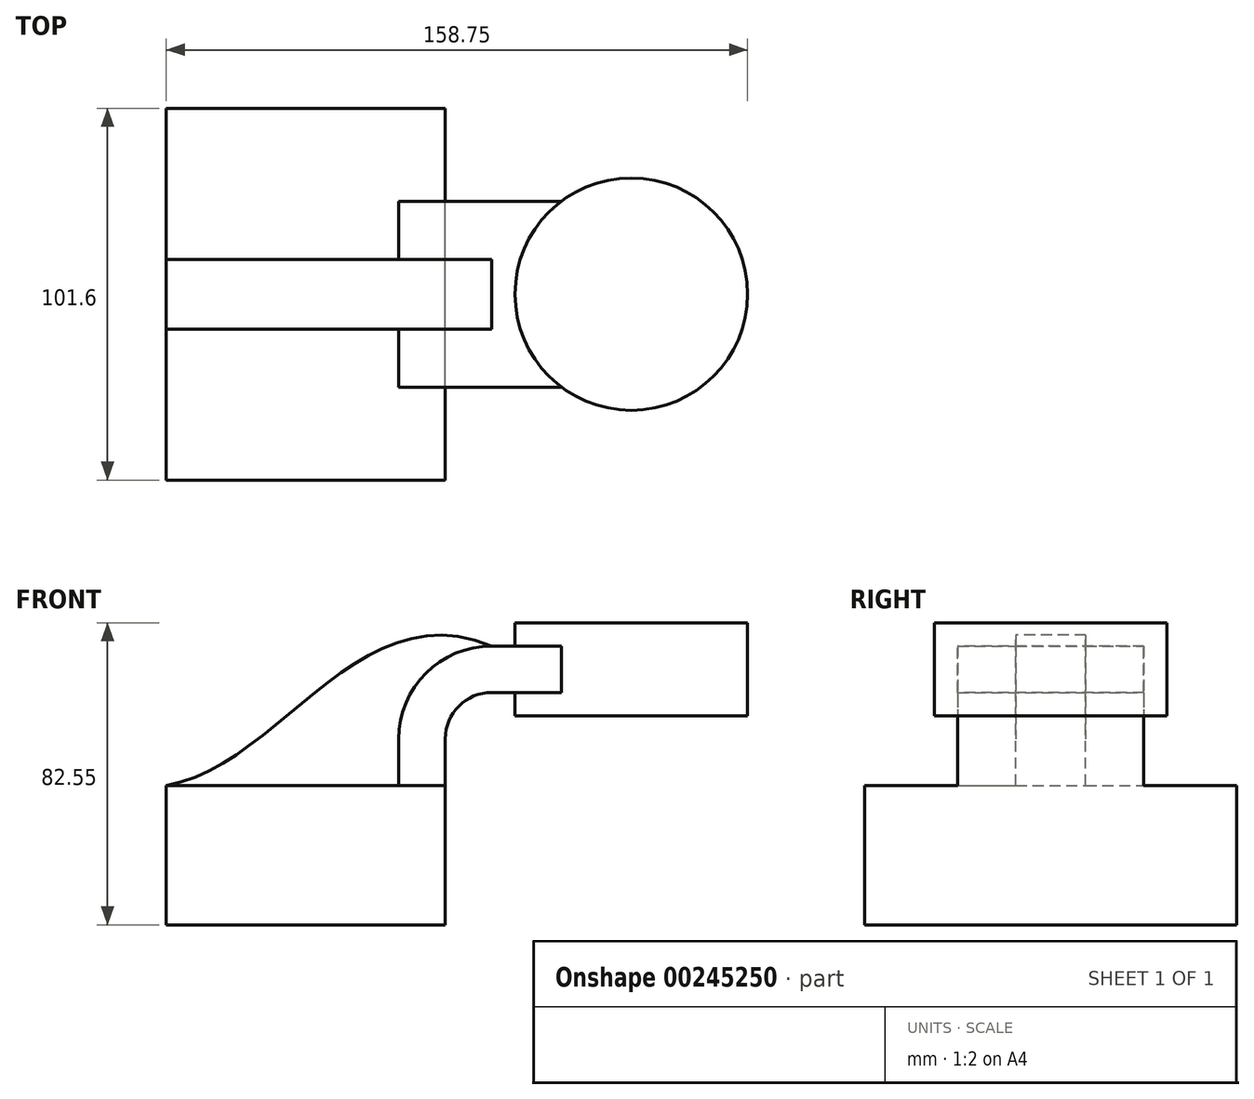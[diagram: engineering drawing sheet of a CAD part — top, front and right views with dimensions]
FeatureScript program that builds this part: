
annotation { "Feature Type Name" : "Feature", "Feature Type Description" : "" }
export const myFeature = defineFeature(function(context is Context, id is Id, definition is map)
    precondition{}
    {
        {
            var Q0;
            Q0=qCreatedBy(makeId("Front.planeOp"),FACE);
            var sketch = newSketch(context, id + "F0", { "sketchPlane" : qUnion([Q0])});
            skLineSegment(sketch, "E0.bottom", {"start": v(38.1, -19.05) * mm, "end": v(-38.1, -19.05) * mm});
            skLineSegment(sketch, "E0.top", {"start": v(38.1, 19.05) * mm, "end": v(-38.1, 19.05) * mm});
            skLineSegment(sketch, "E0.left", {"start": v(38.1, -19.05) * mm, "end": v(38.1, 19.05) * mm});
            skLineSegment(sketch, "E0.right", {"start": v(-38.1, -19.05) * mm, "end": v(-38.1, 19.05) * mm});
            skPoint(sketch, "E0.middle", {"position": v(0, 0) * mm});
            skLineSegment(sketch, "E1.bottom", {"start": v(120.65, 38.1) * mm, "end": v(57.15, 38.1) * mm});
            skLineSegment(sketch, "E1.top", {"start": v(120.65, 63.5) * mm, "end": v(57.15, 63.5) * mm});
            skLineSegment(sketch, "E1.left", {"start": v(120.65, 38.1) * mm, "end": v(120.65, 63.5) * mm});
            skLineSegment(sketch, "E1.right", {"start": v(57.15, 38.1) * mm, "end": v(57.15, 63.5) * mm});
            skPoint(sketch, "E1.middle", {"position": v(88.9, 50.8) * mm});
            skLineSegment(sketch, "E2", {"start": v(38.1, 19.05) * mm, "end": v(38.1, 31.75) * mm});
            skArc(sketch, "E3", {"start": v(50.8, 44.45) * mm, "mid": v(41.82, 40.73) * mm, "end": v(38.1, 31.75) * mm});
            skLineSegment(sketch, "E4", {"start": v(50.8, 44.45) * mm, "end": v(88.9, 44.45) * mm});
            skLineSegment(sketch, "E5.0", {"start": v(50.8, 57.15) * mm, "end": v(88.9, 57.15) * mm});
            skArc(sketch, "E5.1", {"start": v(50.8, 57.15) * mm, "mid": v(32.84, 49.71) * mm, "end": v(25.4, 31.75) * mm});
            skLineSegment(sketch, "E5.2", {"start": v(25.4, 19.05) * mm, "end": v(25.4, 31.75) * mm});
            skLineSegment(sketch, "E6", {"start": v(88.9, 57.15) * mm, "end": v(88.9, 44.45) * mm});
            skFitSpline(sketch, "E7", {"points": [v(-38.1, 19.05) * mm, v(50.8, 57.15) * mm], "startDerivative": vector(93.43, 15.53) * mm, "endDerivative": vector(110.2, -45.74) * mm});
            skLineSegment(sketch, "E8", {"start": v(88.9, 57.15) * mm, "end": v(88.9, 63.5) * mm});
            skLineSegment(sketch, "E9", {"start": v(88.9, 44.45) * mm, "end": v(88.9, 38.1) * mm});
            skSolve(sketch);
        }
        {
            var Q0;
            Q0=makeQuery(id+"F0.imprint","IMPRINT",FACE,{"disambiguationData":[TD([[makeQuery(id+"F0.imprint","IMPRINT",EDGE,{"derivedFrom":sQuery(id+"F0.wireOp",EDGE,"E0.bottom")}),-1.0]])]});
            extrude(context, id + "F1", {"entities" : qUnion([Q0]), "endBound" : BoundingType.SYMMETRIC, "depth" : 101.6 * mm});
        }
        {
            var Q0;
            {var subQ1=sQuery(id+"F0.wireOp",EDGE,"E2");Q0=makeQuery(id+"F0.imprint","IMPRINT",FACE,{"disambiguationData":[TD([[makeQuery(id+"F0.imprint","IMPRINT",EDGE,{"derivedFrom":subQ1}),1.0]])]});}
            var Q1;
            {var subQ5=sQuery(id+"F0.wireOp",EDGE,"E6");Q1=makeQuery(id+"F0.imprint","IMPRINT",FACE,{"disambiguationData":[TD([[makeQuery(id+"F0.imprint","IMPRINT",EDGE,{"derivedFrom":subQ5}),-1.0]])]});}
            extrude(context, id + "F2", {"entities" : qUnion([Q0, Q1]), "operationType" : NewBodyOperationType.ADD, "endBound" : BoundingType.SYMMETRIC, "depth" : 50.8 * mm});
        }
        {
            var Q0;
            {var subQ3=sQuery(id+"F0.wireOp",EDGE,"E5.2");Q0=makeQuery(id+"F0.imprint","IMPRINT",FACE,{"disambiguationData":[TD([[makeQuery(id+"F0.imprint","IMPRINT",EDGE,{"derivedFrom":subQ3}),1.0]])]});}
            extrude(context, id + "F3", {"entities" : qUnion([Q0]), "operationType" : NewBodyOperationType.ADD, "endBound" : BoundingType.SYMMETRIC, "depth" : 19.05 * mm});
        }
        {
            var Q0;
            {var subQ0=sQuery(id+"F0.wireOp",EDGE,"E1.left");Q0=makeQuery(id+"F0.imprint","IMPRINT",FACE,{"disambiguationData":[TD([[makeQuery(id+"F0.imprint","IMPRINT",EDGE,{"derivedFrom":subQ0}),1.0]])]});}
            var Q1;
            Q1=sQuery(id+"F0.wireOp",EDGE,"E6");
            revolve(context, id + "F4", {"operationType" : NewBodyOperationType.ADD, "entities" : qUnion([Q0]), "axis" : qUnion([Q1]), "revolveType" : RevolveType.FULL});
        }
    });
